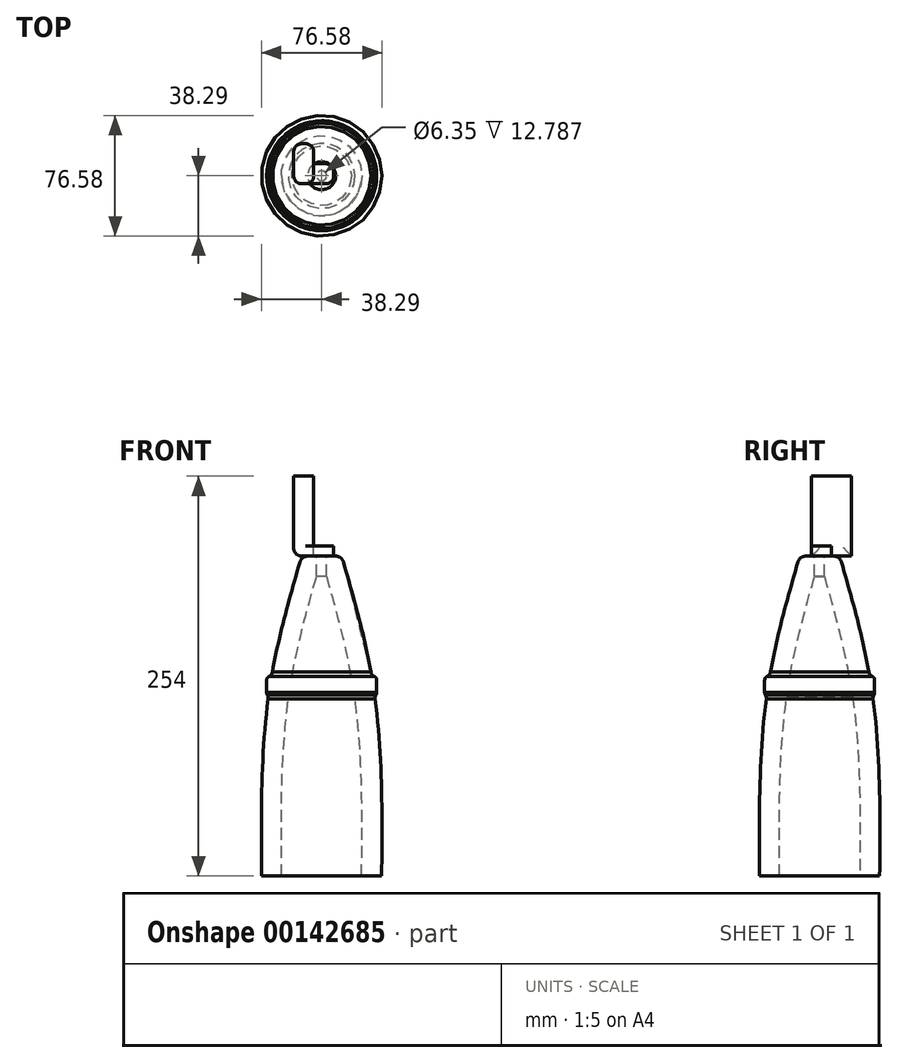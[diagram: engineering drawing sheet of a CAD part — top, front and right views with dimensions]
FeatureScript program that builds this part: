
annotation { "Feature Type Name" : "Feature", "Feature Type Description" : "" }
export const myFeature = defineFeature(function(context is Context, id is Id, definition is map)
    precondition{}
    {
        {
            var Q0;
            Q0=qCreatedBy(makeId("Top.planeOp"),FACE);
            var sketch = newSketch(context, id + "F0", { "sketchPlane" : qUnion([Q0])});
            skCircle(sketch, "E0", {"center": v(0, 0) * mm, "radius": 38.1 * mm});
            skSolve(sketch);
        }
        {
            var Q0;
            Q0=qCreatedBy(makeId("Top.planeOp"),FACE);
            cPlane(context, id + "F1", {"entities" : qUnion([Q0]), "cplaneType" : CPlaneType.OFFSET, "offset" : 203.2 * mm, "width" : 152.4 * mm, "height" : 152.4 * mm});
        }
        {
            var Q0;
            Q0=qCreatedBy(id+"F1.planeOp",FACE);
            var sketch = newSketch(context, id + "F2", { "sketchPlane" : qUnion([Q0])});
            skCircle(sketch, "E1", {"center": v(0, 0) * mm, "radius": 12.7 * mm});
            skSolve(sketch);
        }
        {
            var Q0;
            Q0=qCreatedBy(makeId("Top.planeOp"),FACE);
            cPlane(context, id + "F3", {"entities" : qUnion([Q0]), "cplaneType" : CPlaneType.OFFSET, "offset" : 127 * mm, "width" : 152.4 * mm, "height" : 152.4 * mm});
        }
        {
            var Q0;
            Q0=qCreatedBy(id+"F3.planeOp",FACE);
            var sketch = newSketch(context, id + "F4", { "sketchPlane" : qUnion([Q0])});
            skCircle(sketch, "E2", {"center": v(0, 0) * mm, "radius": 31.75 * mm});
            skSolve(sketch);
        }
        {
            var Q0;
            Q0=makeQuery(id+"F0.imprint","IMPRINT",FACE,{"disambiguationData":[TD([[makeQuery(id+"F0.imprint","IMPRINT",EDGE,{"derivedFrom":sQuery(id+"F0.wireOp",EDGE,"E0")}),1.0]])]});
            var Q1;
            Q1=makeQuery(id+"F4.imprint","IMPRINT",FACE,{"disambiguationData":[TD([[makeQuery(id+"F4.imprint","IMPRINT",EDGE,{"derivedFrom":sQuery(id+"F4.wireOp",EDGE,"E2")}),1.0]])]});
            var Q2;
            Q2=makeQuery(id+"F2.imprint","IMPRINT",FACE,{"disambiguationData":[TD([[makeQuery(id+"F2.imprint","IMPRINT",EDGE,{"derivedFrom":sQuery(id+"F2.wireOp",EDGE,"E1")}),1.0]])]});
            loft(context, id + "F5", {"sheetProfilesArray" : [{ "sheetProfileEntities" : qUnion([Q0]) }, { "sheetProfileEntities" : qUnion([Q1]) }, { "sheetProfileEntities" : qUnion([Q2]) }]});
        }
        {
            var Q0;
            Q0=makeQuery(id+"F5.opLoft","CAP_FACE",FACE,{"disambiguationData":[OSD([makeQuery(id+"F0.imprint","IMPRINT",FACE,{"disambiguationData":[TD([[makeQuery(id+"F0.imprint","IMPRINT",EDGE,{"derivedFrom":sQuery(id+"F0.wireOp",EDGE,"E0")}),1.0]])]})])],"isStart":true});
            shell(context, id + "F6", {"entities" : qUnion([Q0]), "thickness" : 12.7 * mm});
        }
        {
            var Q0;
            Q0=makeQuery(id+"F5.opLoft","CAP_FACE",FACE,{"disambiguationData":[OSD([makeQuery(id+"F2.imprint","IMPRINT",FACE,{"disambiguationData":[TD([[makeQuery(id+"F2.imprint","IMPRINT",EDGE,{"derivedFrom":sQuery(id+"F2.wireOp",EDGE,"E1")}),1.0]])]})])],"isStart":true});
            var sketch = newSketch(context, id + "F7", { "sketchPlane" : qUnion([Q0])});
            skCircle(sketch, "E3", {"center": v(0, 0) * mm, "radius": 3.18 * mm});
            skSolve(sketch);
        }
        {
            var Q0;
            Q0=makeQuery(id+"F7.imprint","IMPRINT",FACE,{"disambiguationData":[TD([[makeQuery(id+"F7.imprint","IMPRINT",EDGE,{"derivedFrom":sQuery(id+"F7.wireOp",EDGE,"E3")}),1.0]])]});
            extrude(context, id + "F8", {"entities" : qUnion([Q0]), "operationType" : NewBodyOperationType.REMOVE, "endBound" : BoundingType.THROUGH_ALL, "oppositeDirection" : true, "depth" : 25.4 * mm});
        }
        {
            var Q0;
            Q0=makeQuery(id+"F5.opLoft","MID_CAP_EDGE",EDGE,{"disambiguationData":[OSD([sQuery(id+"F0.wireOp",EDGE,"E0"),sQuery(id+"F2.wireOp",EDGE,"E1")])],"capPos":2.0});
            fillet(context, id + "F9", {"entities" : qUnion([Q0]), "radius" : 5.08 * mm, "tangentPropagation" : true, "allowEdgeOverflow" : false});
        }
        {
            var Q0;
            Q0=qCreatedBy(id+"F3.planeOp",FACE);
            var sketch = newSketch(context, id + "F10", { "sketchPlane" : qUnion([Q0])});
            skCircle(sketch, "E4", {"center": v(0, 0) * mm, "radius": 34.93 * mm});
            skSolve(sketch);
        }
        {
            var Q0;
            Q0=makeQuery(id+"F10.imprint","IMPRINT",FACE,{"disambiguationData":[TD([[makeQuery(id+"F10.imprint","IMPRINT",EDGE,{"derivedFrom":sQuery(id+"F10.wireOp",EDGE,"E4")}),1.0]])]});
            extrude(context, id + "F11", {"entities" : qUnion([Q0]), "operationType" : NewBodyOperationType.ADD, "oppositeDirection" : true, "depth" : 12.7 * mm});
        }
        {
            var Q0;
            Q0=makeQuery(id+"F11.opExtrude","CAP_EDGE",EDGE,{"disambiguationData":[OSD([sQuery(id+"F10.wireOp",EDGE,"E4")])],"isStart":true});
            var Q1;
            Q1=makeQuery(id+"F11.opExtrude","CAP_EDGE",EDGE,{"disambiguationData":[OSD([sQuery(id+"F10.wireOp",EDGE,"E4")])],"isStart":false});
            fillet(context, id + "F12", {"entities" : qUnion([Q0, Q1]), "radius" : 2.54 * mm, "tangentPropagation" : true, "allowEdgeOverflow" : false});
        }
        {
            var Q0;
            Q0=makeQuery(id+"F11.boolean.opBoolean","INTERSECT",EDGE,{"derivedFrom":[makeQuery(id+"F5.opLoft","SWEPT_FACE",FACE,{"disambiguationData":[OSD([sQuery(id+"F0.wireOp",EDGE,"E0"),sQuery(id+"F4.wireOp",EDGE,"E2")])]}),makeQuery(id+"F11.opExtrude","CAP_FACE",FACE,{"disambiguationData":[OSD([sQuery(id+"F10.wireOp",EDGE,"E4")])],"isStart":true})]});
            var Q1;
            {var subQ0=sQuery(id+"F0.wireOp",EDGE,"E0");var subQ1=sQuery(id+"F10.wireOp",EDGE,"E4");Q1=makeQuery(id+"F12.opFillet","BLEND_EDGE",EDGE,{"blendedFrom":[makeQuery(id+"F11.opExtrude","CAP_EDGE",EDGE,{"disambiguationData":[OSD([subQ1])],"isStart":false}),makeQuery(id+"F11.boolean.opBoolean","SPLIT",FACE,{"disambiguationData":[TD([makeQuery(id+"F5.opLoft","CAP_FACE",FACE,{"disambiguationData":[OSD([makeQuery(id+"F0.imprint","IMPRINT",FACE,{"disambiguationData":[TD([[makeQuery(id+"F0.imprint","IMPRINT",EDGE,{"derivedFrom":subQ0}),1.0]])]})])],"isStart":true})])],"derivedFrom":makeQuery(id+"F5.opLoft","SWEPT_FACE",FACE,{"disambiguationData":[OSD([subQ0,sQuery(id+"F4.wireOp",EDGE,"E2")])]})})],"blendedInto":[makeQuery(id+"F11.boolean.opBoolean","SPLIT",FACE,{"disambiguationData":[TD([makeQuery(id+"F5.opLoft","CAP_FACE",FACE,{"disambiguationData":[OSD([makeQuery(id+"F0.imprint","IMPRINT",FACE,{"disambiguationData":[TD([[makeQuery(id+"F0.imprint","IMPRINT",EDGE,{"derivedFrom":subQ0}),1.0]])]})])],"isStart":true})])],"derivedFrom":makeQuery(id+"F5.opLoft","SWEPT_FACE",FACE,{"disambiguationData":[OSD([subQ0,sQuery(id+"F4.wireOp",EDGE,"E2")])]})})]});}
            fillet(context, id + "F13", {"entities" : qUnion([Q0, Q1]), "radius" : 3.8 * mm, "tangentPropagation" : true, "allowEdgeOverflow" : false});
        }
        {
            var Q0;
            Q0=qCreatedBy(id+"F1.planeOp",FACE);
            var sketch = newSketch(context, id + "F14", { "sketchPlane" : qUnion([Q0])});
            skLineSegment(sketch, "E5.bottom", {"start": v(-5.08, -5.08) * mm, "end": v(-17.78, -5.08) * mm});
            skLineSegment(sketch, "E5.top", {"start": v(-5.08, 20.32) * mm, "end": v(-17.78, 20.32) * mm});
            skLineSegment(sketch, "E5.left", {"start": v(-5.08, -5.08) * mm, "end": v(-5.08, 20.32) * mm});
            skLineSegment(sketch, "E5.right", {"start": v(-17.78, -5.08) * mm, "end": v(-17.78, 20.32) * mm});
            skSolve(sketch);
        }
        {
            var Q0;
            Q0=makeQuery(id+"F14.imprint","IMPRINT",FACE,{"disambiguationData":[TD([[makeQuery(id+"F14.imprint","IMPRINT",EDGE,{"derivedFrom":sQuery(id+"F14.wireOp",EDGE,"E5.bottom")}),-1.0]])]});
            extrude(context, id + "F15", {"entities" : qUnion([Q0]), "operationType" : NewBodyOperationType.ADD, "depth" : 50.8 * mm});
        }
        {
            var Q0;
            Q0=makeQuery(id+"F15.opExtrude","SWEPT_FACE",FACE,{"disambiguationData":[OSD([sQuery(id+"F14.wireOp",EDGE,"E5.left")])]});
            var sketch = newSketch(context, id + "F16", { "sketchPlane" : qUnion([Q0])});
            skLineSegment(sketch, "E6.bottom", {"start": v(-5.08, 203.2) * mm, "end": v(7.62, 203.2) * mm});
            skLineSegment(sketch, "E6.top", {"start": v(-5.08, 209.55) * mm, "end": v(7.62, 209.55) * mm});
            skLineSegment(sketch, "E6.left", {"start": v(-5.08, 203.2) * mm, "end": v(-5.08, 209.55) * mm});
            skLineSegment(sketch, "E6.right", {"start": v(7.62, 203.2) * mm, "end": v(7.62, 209.55) * mm});
            skSolve(sketch);
        }
        {
            var Q0;
            Q0=makeQuery(id+"F16.imprint","IMPRINT",FACE,{"disambiguationData":[TD([[makeQuery(id+"F16.imprint","IMPRINT",EDGE,{"derivedFrom":sQuery(id+"F16.wireOp",EDGE,"E6.top")}),-1.0]])]});
            extrude(context, id + "F17", {"entities" : qUnion([Q0]), "operationType" : NewBodyOperationType.ADD, "depth" : 12.7 * mm});
        }
        {
            var Q0;
            Q0=makeQuery(id+"F17.opExtrude","CAP_EDGE",EDGE,{"disambiguationData":[OSD([sQuery(id+"F16.wireOp",EDGE,"E6.right")])],"isStart":false});
            var Q1;
            Q1=makeQuery(id+"F17.opExtrude","CAP_EDGE",EDGE,{"disambiguationData":[OSD([sQuery(id+"F16.wireOp",EDGE,"E6.left")])],"isStart":false});
            var Q2;
            Q2=makeQuery(id+"F17.opExtrude","CAP_EDGE",EDGE,{"disambiguationData":[OSD([sQuery(id+"F16.wireOp",EDGE,"E6.right")])],"isStart":true});
            var Q3;
            Q3=makeQuery(id+"F17.opExtrude","CAP_EDGE",EDGE,{"disambiguationData":[OSD([sQuery(id+"F16.wireOp",EDGE,"E6.top")])],"isStart":true});
            var Q4;
            Q4=makeQuery(id+"F15.opExtrude","SWEPT_EDGE",EDGE,{"disambiguationData":[OSD([sQuery(id+"F14.wireOp",EDGE,"E5.bottom"),sQuery(id+"F14.wireOp",EDGE,"E5.right")])]});
            var Q5;
            Q5=makeQuery(id+"F15.opExtrude","SWEPT_EDGE",EDGE,{"disambiguationData":[OSD([sQuery(id+"F14.wireOp",EDGE,"E5.top"),sQuery(id+"F14.wireOp",EDGE,"E5.right")])]});
            var Q6;
            Q6=makeQuery(id+"F15.opExtrude","CAP_EDGE",EDGE,{"disambiguationData":[OSD([sQuery(id+"F14.wireOp",EDGE,"E5.right")])],"isStart":true});
            var Q7;
            Q7=makeQuery(id+"F15.opExtrude","SWEPT_EDGE",EDGE,{"disambiguationData":[OSD([sQuery(id+"F14.wireOp",EDGE,"E5.top"),sQuery(id+"F14.wireOp",EDGE,"E5.left")])]});
            var Q8;
            Q8=makeQuery(id+"F15.opExtrude","SWEPT_EDGE",EDGE,{"disambiguationData":[OSD([sQuery(id+"F14.wireOp",EDGE,"E5.bottom"),sQuery(id+"F14.wireOp",EDGE,"E5.left")])]});
            fillet(context, id + "F18", {"entities" : qUnion([Q0, Q1, Q2, Q3, Q4, Q5, Q6, Q7, Q8]), "radius" : 5.08 * mm, "tangentPropagation" : true, "allowEdgeOverflow" : false});
        }
    });
